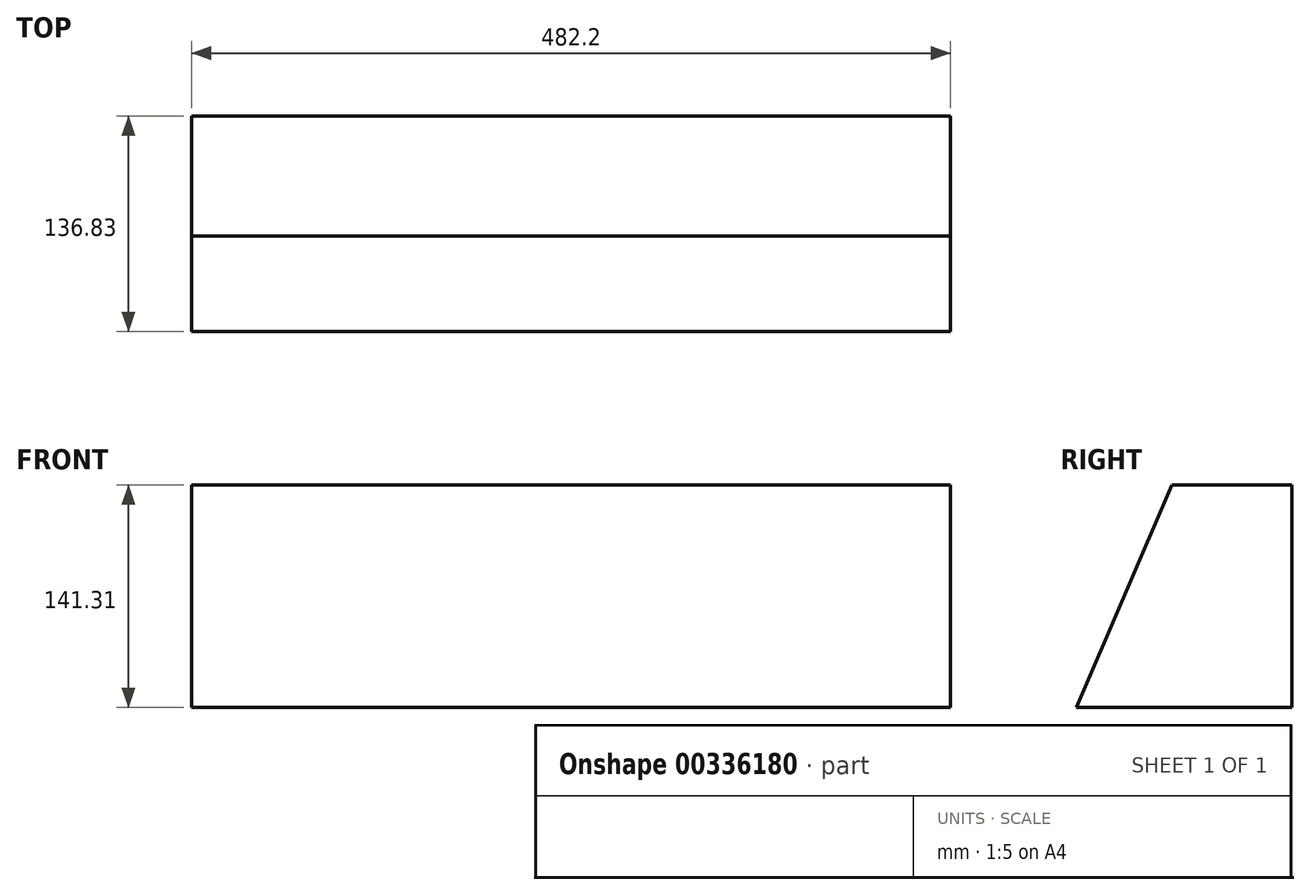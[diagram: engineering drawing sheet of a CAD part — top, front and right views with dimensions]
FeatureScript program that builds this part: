
annotation { "Feature Type Name" : "Feature", "Feature Type Description" : "" }
export const myFeature = defineFeature(function(context is Context, id is Id, definition is map)
    precondition{}
    {
        {
            var Q0;
            Q0=qCreatedBy(makeId("Right.planeOp"),FACE);
            var sketch = newSketch(context, id + "F0", { "sketchPlane" : qUnion([Q0])});
            skLineSegment(sketch, "E0", {"start": v(0, 0) * mm, "end": v(76.32, 0) * mm});
            skLineSegment(sketch, "E1", {"start": v(76.32, 0) * mm, "end": v(76.32, -141.31) * mm});
            skLineSegment(sketch, "E2", {"start": v(76.32, -141.31) * mm, "end": v(-60.51, -141.31) * mm});
            skLineSegment(sketch, "E3", {"start": v(-60.51, -141.31) * mm, "end": v(0, 0) * mm});
            skSolve(sketch);
        }
        {
            var Q0;
            Q0=makeQuery(id+"F0.imprint","IMPRINT",FACE,{"disambiguationData":[TD([[makeQuery(id+"F0.imprint","IMPRINT",EDGE,{"derivedFrom":sQuery(id+"F0.wireOp",EDGE,"E0")}),-1.0]])]});
            extrude(context, id + "F1", {"entities" : qUnion([Q0]), "oppositeDirection" : true, "depth" : 482.2 * mm});
        }
    });
